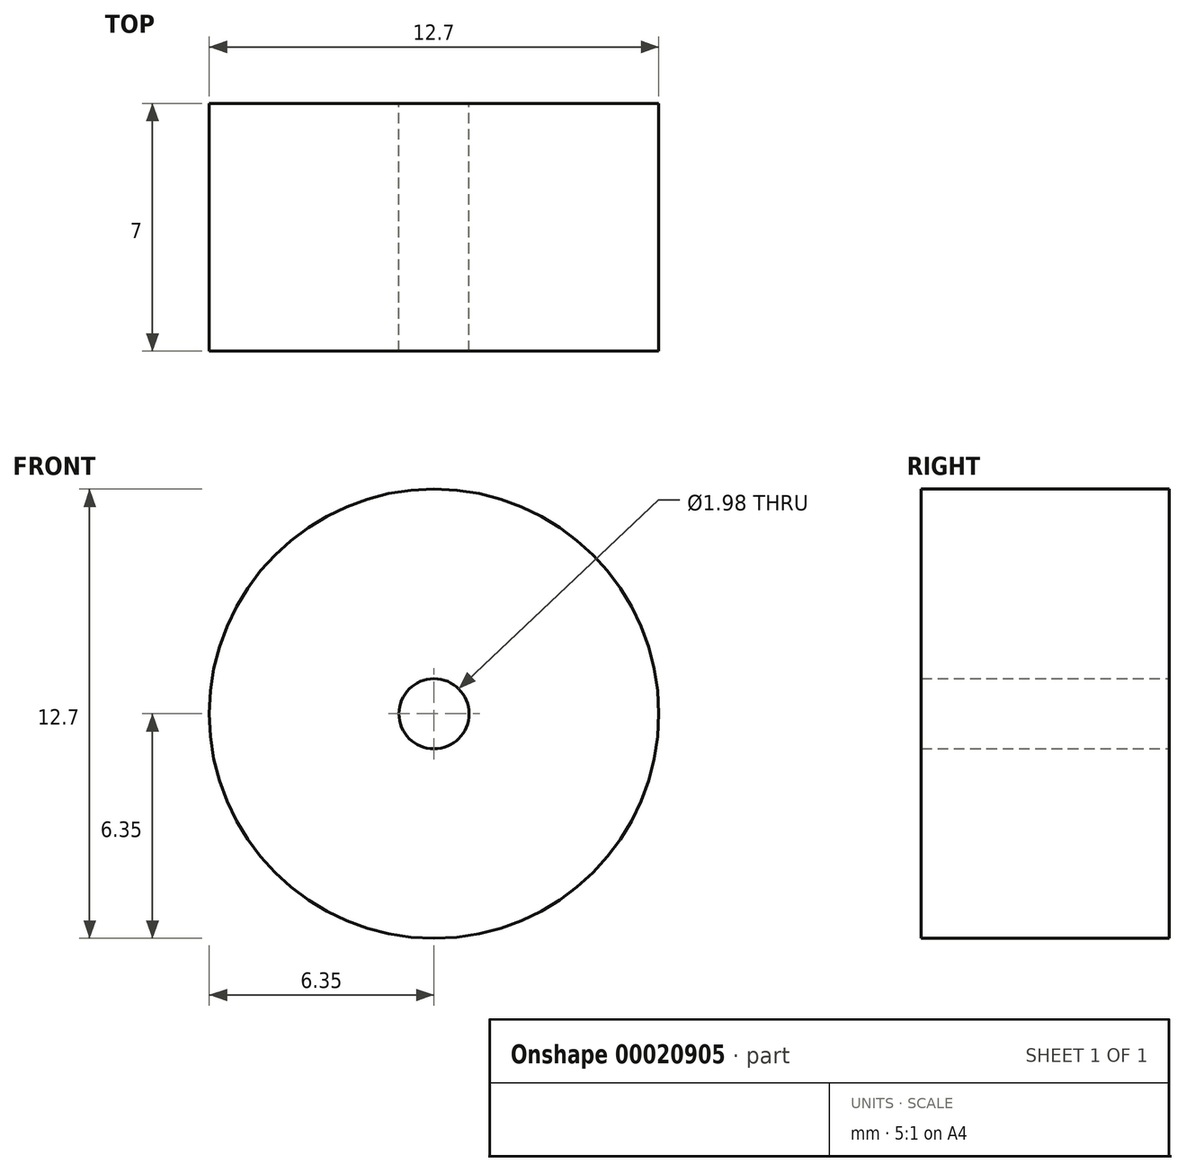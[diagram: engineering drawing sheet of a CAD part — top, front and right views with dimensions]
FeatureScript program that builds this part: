
annotation { "Feature Type Name" : "Feature", "Feature Type Description" : "" }
export const myFeature = defineFeature(function(context is Context, id is Id, definition is map)
    precondition{}
    {
        {
            var Q0;
            Q0=qCreatedBy(makeId("Front.planeOp"),FACE);
            var sketch = newSketch(context, id + "F0", { "sketchPlane" : qUnion([Q0])});
            skCircle(sketch, "E0", {"center": v(0, 0) * mm, "radius": 1 * mm});
            skCircle(sketch, "E1", {"center": v(0, 0) * mm, "radius": 6.35 * mm});
            skSolve(sketch);
        }
        {
            var Q0;
            Q0=makeQuery(id+"F0.imprint","IMPRINT",FACE,{"disambiguationData":[TD([[makeQuery(id+"F0.imprint","IMPRINT",EDGE,{"derivedFrom":sQuery(id+"F0.wireOp",EDGE,"E0")}),-1.0]])]});
            extrude(context, id + "F1", {"entities" : qUnion([Q0]), "depth" : 7 * mm});
        }
    });
